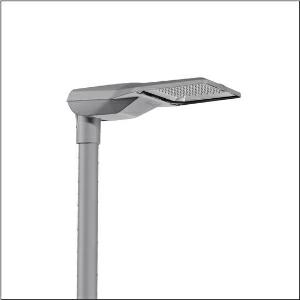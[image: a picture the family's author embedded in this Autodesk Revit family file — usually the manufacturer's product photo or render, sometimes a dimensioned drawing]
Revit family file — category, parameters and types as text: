
# Revit family: streetlight_sl_21_iq_midi___st0_8a_5xe3c31d08mb_7ea8
name_source: partatom
category: Lighting Fixtures
units: mm (PartAtom-declared; Revit-internal decimal feet)

## family parameters
Cut with Voids When Loaded = No
Host = Face
Light Source = No
Part Type = Normal
Room Calculation Point = No
Round Connector Dimension = Use Diameter
Shared = No

## types (1)
- --- (1 x LED, 19500 lm, 146.7 W, 3000K)
    Apparent Load = 147 VA
    CIE Flux Codes = 38 75 97 100 100
    Color Rendering = 70
    Color Temperature = 3000K
    Default Elevation = 1800 mm
    Description = Streetlight SL 21 iQ midi, mast luminaire, primary light control with lens, of PMMA, primary optical cover: cover, of toughened safety glass, transparent, light distribution: ST0.8a, light emission: direct distribution, primary light characteristic: asymmetric, installation type: post-top, side-entry, LED, High Power LED, rated luminous flux: 19.500lm, luminous efficacy: 133lm/W, light colour: 730, colour temperature: 3000K, control: Auto-Match, Temp-Guard, Lumen-Switch, Night-Set, Smart-Wire, Light-Fading, Desk-Remote (wireless, voltage-free reading and setting of iQ features in the workshop via application-optimized NFC function/RFID function), optimised constant luminous flux control (CLO 2.0), presetting dimming linear, mains connection: 230..240V, AC, 50/60Hz, start of lifetime: 147W, end of service life: 161W, reduction: 62W, luminaire housing, of diecast aluminium, powder-coated, Siteco® metallic grey (DB 702S), corrosivity category C5 mid according to DIN EN ISO 12944, please order mast flange separately, inclination adjustable: 0°, 5°, 10°, 15°, sealing non-destructively replaceable, multi-level sealing system, length: 644mm, width: 335mm, height: 110mm, mast flange for spigot size: 42mm (side-entry): 5XC10008XM4, 60/48mm (side-entry/post-top): 5XC10108XM2, 76/60mm (side-entry/post-top): 5XC10108XM1, protection rating (complete): IP66, insulation class (complete): insulation class II (safety insulation), certification: CE, ENEC, ENEC+, VDE, impact resistance: IK09, permissible operating ambient temperature for outdoor applications: -40..+50°C, standard-compliant lighting for roads and squares, packaging unit: 1 piece

Light Distribution: ST0.8a
    Height = 111 mm
    Lamp = 1 x LED
    Lamp Light Flux = 19500 lm
    Lamp Power = 146.7 W
    Lamp count = 1
    Length = 644 mm
    Luminous efficacy = 133 lm/W
    Manufacturer = Siteco
    ModVariant = No
    Model = 5XE3C31D08MB
    Number of Poles = 1
    OnlyDefault = Yes
    Power Factor = 1
    Product Name = Streetlight SL 21 iQ midi | ST0.8a
    Product group = mast luminaire | pylon top
    ProductGroupID = 6100
    Protection Class = Protection class II
    Protection Degree = IP 66
    RLX_Detail_Level = 1
    RLX_Emergency_Light_Flux = 0 lm
    RLX_Emergency_Type = 0
    RLX_Emergency_Type_DB = No
    RlxData = <blob elided: 91021 chars, md5=4365e223>
    Socket = socket
    Standby Power = 0 W
    System Light Flux = 19499 lm
    System Power = 147 W
    Type Comments = factory setting: luminous flux: 100 % | dim-lin: 254 | 753 mA
    Type Image = l_1004298.jpg
    URL = http://relux.com
    VarID = @adj_119755
    Voltage = 0 V
    Weight = 0.00 kg
    Width = 336 mm

## geometry (parser evidence)
native form markers: Blend x4, Sweep x11
no freeform markers — native parametric forms only
